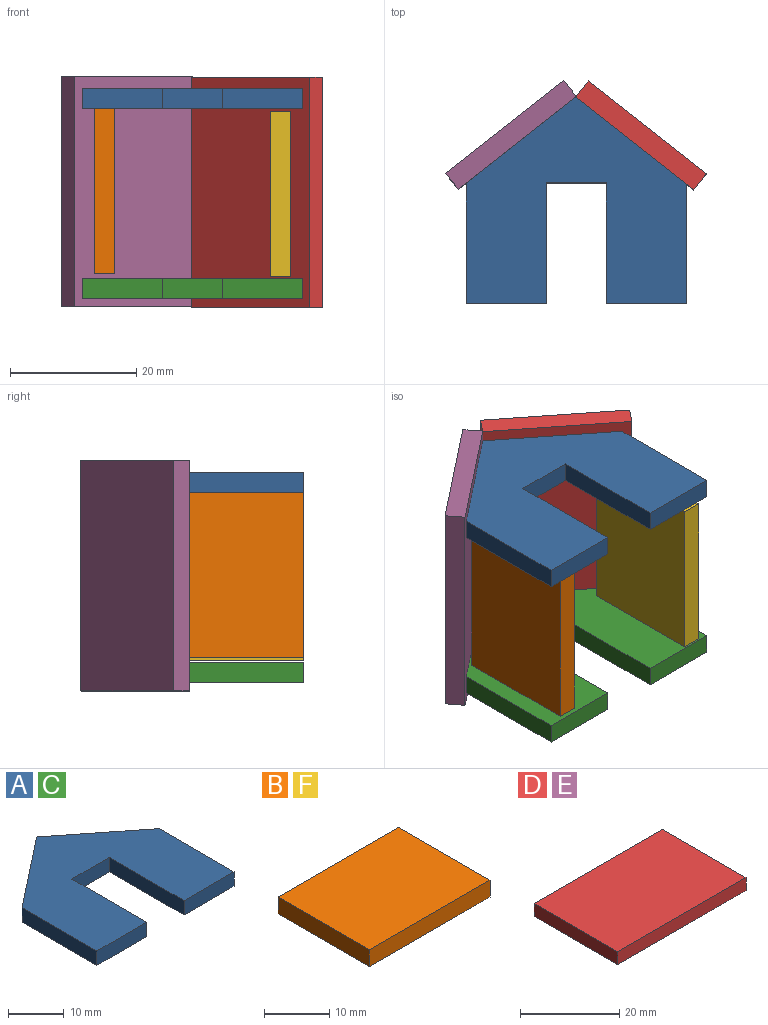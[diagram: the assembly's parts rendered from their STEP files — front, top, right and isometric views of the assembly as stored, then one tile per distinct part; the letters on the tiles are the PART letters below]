
ASSEMBLY  parts=6 mates=4
PART A: 11 faces, bbox 34.9x32.8x3.2 mm
  f0: plane 17.46x13.75mm, normal (0.62,0.79,0), area 70.6mm2, adj f1,f8,f9,f10
  f1: plane 17.46x13.75mm, normal (-0.62,0.79,0), area 70.6mm2, adj f0,f2,f9,f10
  f2: plane 19.05x3.18mm, normal (-1,0,0), area 60.5mm2, adj f1,f3,f9,f10
  f3: plane 12.7x3.18mm, normal (0,-1,0), area 40.3mm2, adj f2,f4,f9,f10
  f4: plane 19.05x3.18mm, normal (1,0,0), area 60.5mm2, adj f3,f5,f9,f10
  f5: plane 9.53x3.18mm, normal (0,-1,0), area 30.2mm2, adj f4,f6,f9,f10
  f6: plane 19.05x3.18mm, normal (-1,0,0), area 60.5mm2, adj f5,f7,f9,f10
  f7: plane 12.7x3.18mm, normal (0,-1,0), area 40.3mm2, adj f6,f8,f9,f10
  f8: plane 19.05x3.18mm, normal (1,0,0), area 60.5mm2, adj f0,f7,f9,f10
  f9: plane 34.93x32.8mm, normal (0,0,1), area 723.9mm2, adj f0,f1,f2,f3,f4,f5,f6,f7
  f10: plane 34.93x32.8mm, normal (0,0,-1), area 723.9mm2, adj f0,f1,f2,f3,f4,f5,f6,f7
PART B: 6 faces, bbox 26.2x19.8x3.2 mm
  f0: plane 26.19x3.18mm, normal (0,-1,0), area 83.2mm2, adj f1,f3,f4,f5
  f1: plane 19.84x3.18mm, normal (1,0,0), area 63mm2, adj f0,f2,f4,f5
  f2: plane 26.19x3.18mm, normal (0,1,0), area 83.2mm2, adj f1,f3,f4,f5
  f3: plane 19.84x3.18mm, normal (-1,0,0), area 63mm2, adj f0,f2,f4,f5
  f4: plane 26.19x19.84mm, normal (0,0,1), area 519.8mm2, adj f0,f1,f2,f3
  f5: plane 26.19x19.84mm, normal (0,0,-1), area 519.8mm2, adj f0,f1,f2,f3
PART C: same geometry as A
PART D: 6 faces, bbox 36.5x23.8x3.2 mm
  f0: plane 36.51x3.18mm, normal (0,-1,0), area 115.9mm2, adj f1,f3,f4,f5
  f1: plane 23.81x3.18mm, normal (1,0,0), area 75.6mm2, adj f0,f2,f4,f5
  f2: plane 36.51x3.18mm, normal (0,1,0), area 115.9mm2, adj f1,f3,f4,f5
  f3: plane 23.81x3.18mm, normal (-1,0,0), area 75.6mm2, adj f0,f2,f4,f5
  f4: plane 36.51x23.81mm, normal (0,0,1), area 869.5mm2, adj f0,f1,f2,f3
  f5: plane 36.51x23.81mm, normal (0,0,-1), area 869.5mm2, adj f0,f1,f2,f3
PART E: same geometry as D
PART F: same geometry as B
PLACE A at identity fixed
PLACE B rot(axis=(0,1,0),90deg) t=(-15.43,-22.88,-13.1)mm
PLACE C t=(0,0,-30.16)mm
PLACE D rot(axis=(0.67,0.32,-0.67),144deg) t=(11.26,-4.94,-13.24)mm
PLACE E rot(axis=(-0.67,0.32,0.67),144deg) t=(-9.35,-7.37,-13.18)mm
PLACE F rot(axis=(0,1,0),90deg) t=(12.47,-22.88,-13.57)mm
MATE slider A.f10 <-> C.f9  axis (0,0,-1) through (0,-18.59,0)mm
MATE planar A.f7 <-> F.f0  axis (0,-1,0) through (11.11,-32.8,1.59)mm
MATE fastened B.f3 <-> A.f10  axis (0,0,1) through (-15.43,-32.8,0)mm
MATE fastened A.f1 <-> E.f5  axis (-0.62,0.79,0) through (0,0,0)mm
